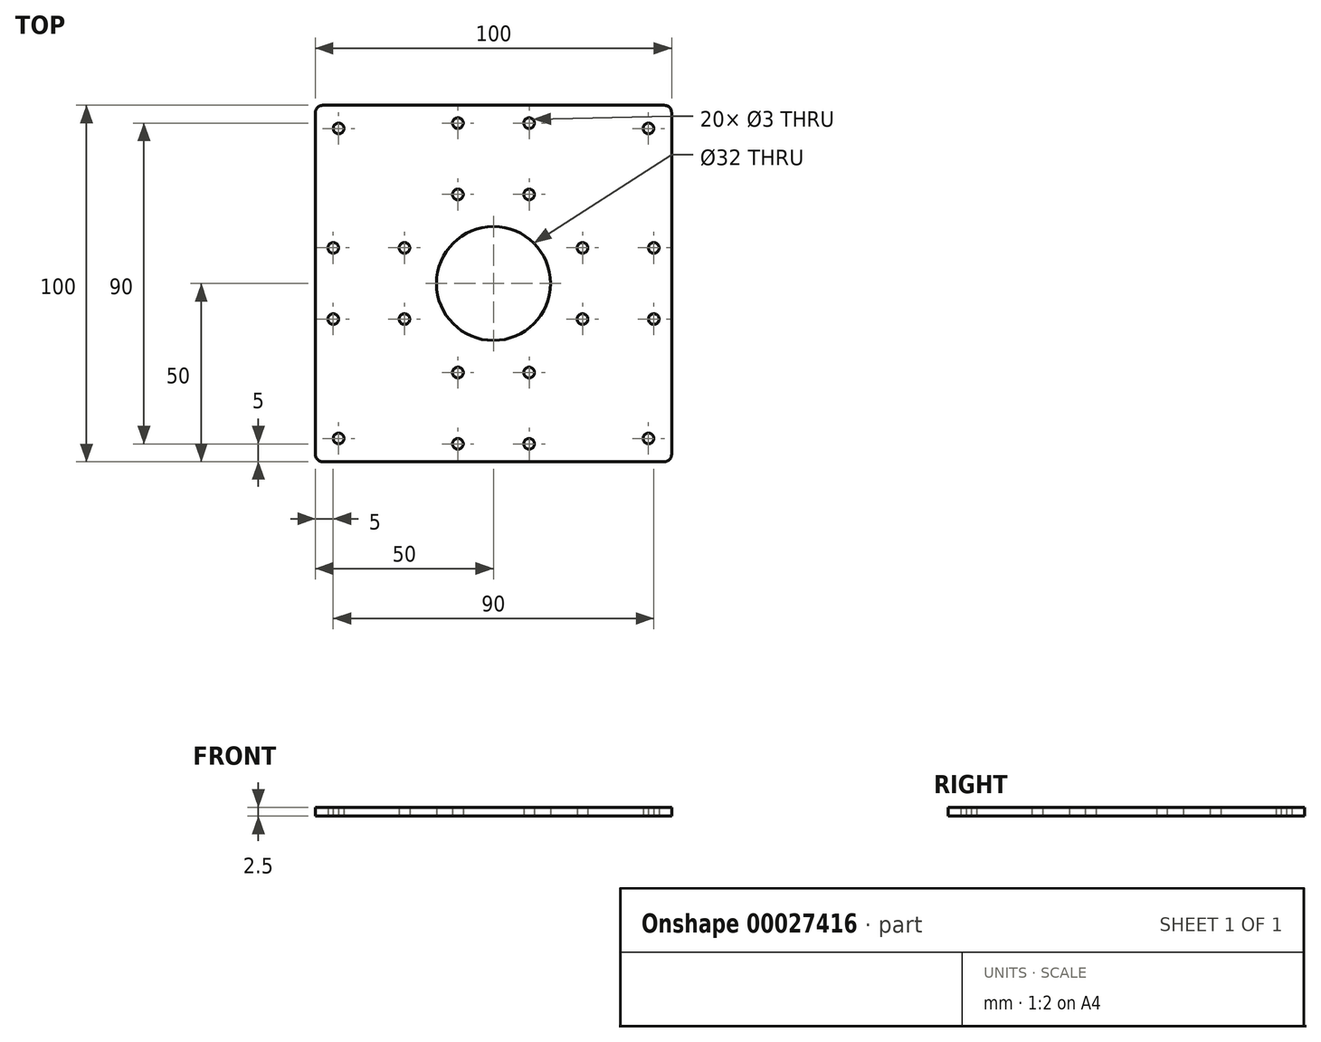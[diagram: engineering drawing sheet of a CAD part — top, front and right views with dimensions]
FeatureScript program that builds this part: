
annotation { "Feature Type Name" : "Feature", "Feature Type Description" : "" }
export const myFeature = defineFeature(function(context is Context, id is Id, definition is map)
    precondition{}
    {
        {
            var Q0;
            Q0=qCreatedBy(makeId("Top.planeOp"),FACE);
            var sketch = newSketch(context, id + "F0", { "sketchPlane" : qUnion([Q0])});
            skLineSegment(sketch, "E0.rect.bottom", {"start": v(50, -50) * mm, "end": v(-50, -50) * mm});
            skLineSegment(sketch, "E0.rect.top", {"start": v(50, 50) * mm, "end": v(-50, 50) * mm});
            skLineSegment(sketch, "E0.rect.left", {"start": v(50, -50) * mm, "end": v(50, 50) * mm});
            skLineSegment(sketch, "E0.rect.right", {"start": v(-50, -50) * mm, "end": v(-50, 50) * mm});
            skPoint(sketch, "E0.rect.middle", {"position": v(0, 0) * mm});
            skCircle(sketch, "E1", {"center": v(0, 0) * mm, "radius": 16 * mm});
            skLineSegment(sketch, "E2", {"start": v(50, 45) * mm, "end": v(-50, 45) * mm, "construction": true});
            skCircle(sketch, "E3", {"center": v(-10, 45) * mm, "radius": 1.5 * mm});
            skCircle(sketch, "E4", {"center": v(10, 45) * mm, "radius": 1.5 * mm});
            skLineSegment(sketch, "E5", {"start": v(-50, 0) * mm, "end": v(50, 0) * mm, "construction": true});
            skCircle(sketch, "E6.MirrorC", {"center": v(-10, -45) * mm, "radius": 1.5 * mm});
            skCircle(sketch, "E7.MirrorC", {"center": v(10, -45) * mm, "radius": 1.5 * mm});
            skLineSegment(sketch, "E8", {"start": v(45, 50) * mm, "end": v(45, -50) * mm, "construction": true});
            skCircle(sketch, "E9", {"center": v(45, 10) * mm, "radius": 1.5 * mm});
            skCircle(sketch, "E10.MirrorC", {"center": v(45, -10) * mm, "radius": 1.5 * mm});
            skLineSegment(sketch, "E11", {"start": v(0, 50) * mm, "end": v(0, -50) * mm, "construction": true});
            skCircle(sketch, "E12.MirrorC", {"center": v(-45, 10) * mm, "radius": 1.5 * mm});
            skCircle(sketch, "E13.MirrorC", {"center": v(-45, -10) * mm, "radius": 1.5 * mm});
            skCircle(sketch, "E14", {"center": v(-43.5, -43.5) * mm, "radius": 1.5 * mm});
            skCircle(sketch, "E15.MirrorC", {"center": v(43.5, -43.5) * mm, "radius": 1.5 * mm});
            skCircle(sketch, "E16.MirrorC", {"center": v(43.5, 43.5) * mm, "radius": 1.5 * mm});
            skCircle(sketch, "E17.MirrorC", {"center": v(-43.5, 43.5) * mm, "radius": 1.5 * mm});
            skCircle(sketch, "E18", {"center": v(-10, 25) * mm, "radius": 1.5 * mm});
            skCircle(sketch, "E19", {"center": v(10, 25) * mm, "radius": 1.5 * mm});
            skCircle(sketch, "E20.MirrorC", {"center": v(-10, -25) * mm, "radius": 1.5 * mm});
            skCircle(sketch, "E21.MirrorC", {"center": v(10, -25) * mm, "radius": 1.5 * mm});
            skCircle(sketch, "E22", {"center": v(-25, 10) * mm, "radius": 1.5 * mm});
            skCircle(sketch, "E23", {"center": v(-25, -10) * mm, "radius": 1.5 * mm});
            skCircle(sketch, "E24.MirrorC", {"center": v(25, 10) * mm, "radius": 1.5 * mm});
            skCircle(sketch, "E25.MirrorC", {"center": v(25, -10) * mm, "radius": 1.5 * mm});
            skSolve(sketch);
        }
        {
            var Q0;
            Q0=makeQuery(id+"F0.imprint","IMPRINT",FACE,{"disambiguationData":[TD([[makeQuery(id+"F0.imprint","IMPRINT",EDGE,{"derivedFrom":sQuery(id+"F0.wireOp",EDGE,"E0.rect.bottom")}),-1.0]])]});
            extrude(context, id + "F1", {"entities" : qUnion([Q0]), "depth" : 2.5 * mm});
        }
        {
            var Q0;
            Q0=makeQuery(id+"F1.opExtrude","SWEPT_EDGE",EDGE,{"disambiguationData":[OSD([sQuery(id+"F0.wireOp",EDGE,"E0.rect.bottom"),sQuery(id+"F0.wireOp",EDGE,"E0.rect.left")])]});
            var Q1;
            Q1=makeQuery(id+"F1.opExtrude","SWEPT_EDGE",EDGE,{"disambiguationData":[OSD([sQuery(id+"F0.wireOp",EDGE,"E0.rect.top"),sQuery(id+"F0.wireOp",EDGE,"E0.rect.left")])]});
            var Q2;
            Q2=makeQuery(id+"F1.opExtrude","SWEPT_EDGE",EDGE,{"disambiguationData":[OSD([sQuery(id+"F0.wireOp",EDGE,"E0.rect.top"),sQuery(id+"F0.wireOp",EDGE,"E0.rect.right")])]});
            var Q3;
            Q3=makeQuery(id+"F1.opExtrude","SWEPT_EDGE",EDGE,{"disambiguationData":[OSD([sQuery(id+"F0.wireOp",EDGE,"E0.rect.bottom"),sQuery(id+"F0.wireOp",EDGE,"E0.rect.right")])]});
            fillet(context, id + "F2", {"entities" : qUnion([Q0, Q1, Q2, Q3]), "radius" : 2 * mm, "tangentPropagation" : true, "allowEdgeOverflow" : false});
        }
    });
